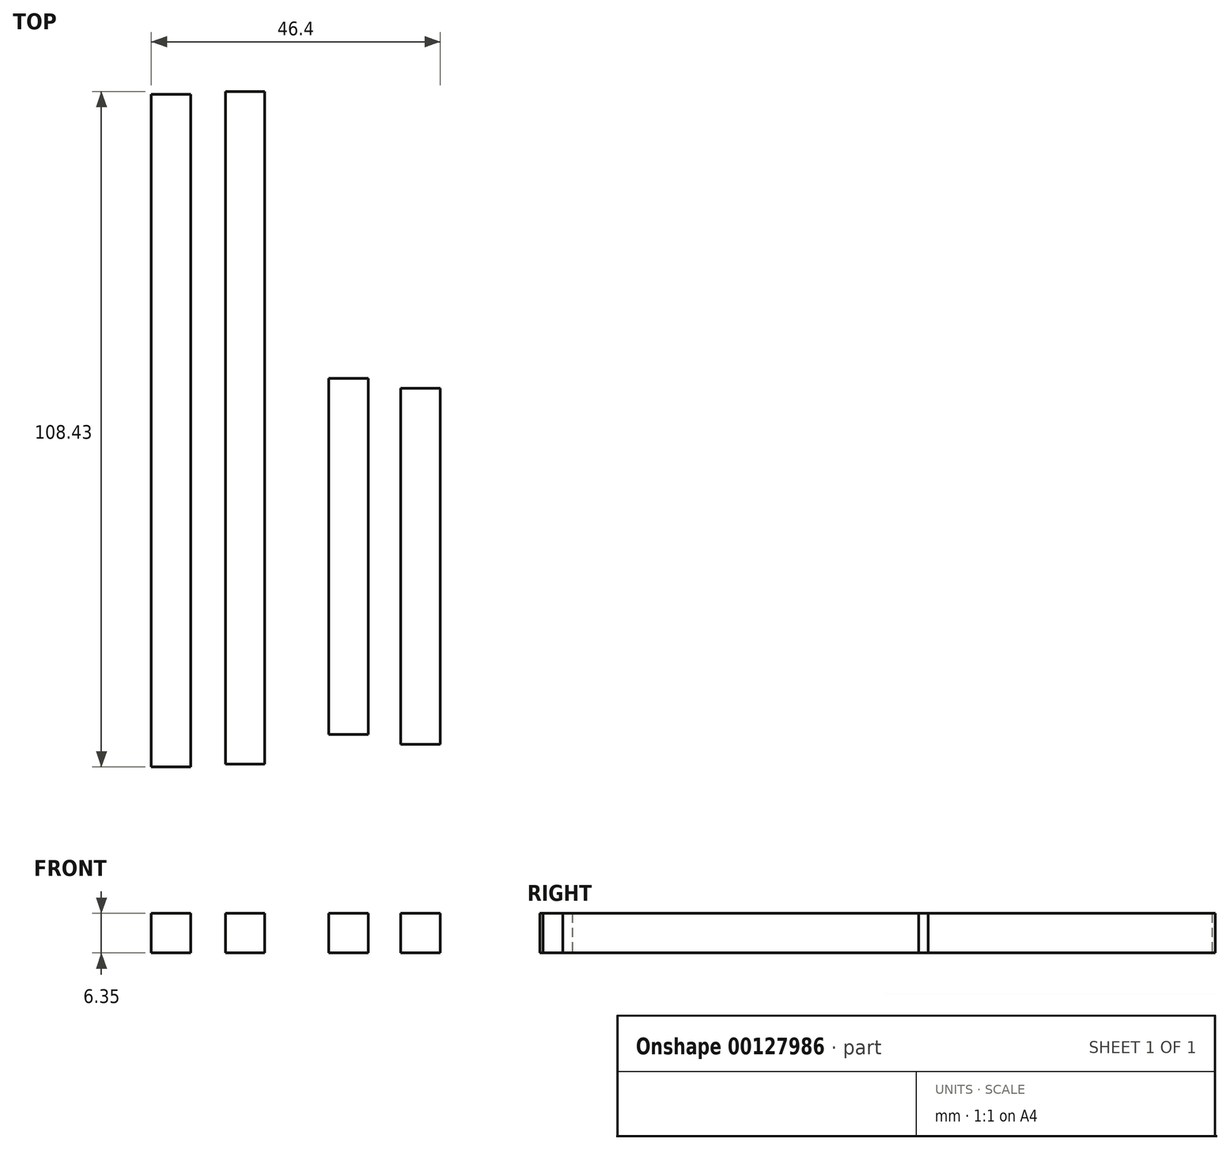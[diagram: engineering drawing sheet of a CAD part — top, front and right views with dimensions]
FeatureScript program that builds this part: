
annotation { "Feature Type Name" : "Feature", "Feature Type Description" : "" }
export const myFeature = defineFeature(function(context is Context, id is Id, definition is map)
    precondition{}
    {
        {
            var Q0;
            Q0=qCreatedBy(makeId("Top.planeOp"),FACE);
            var sketch = newSketch(context, id + "F0", { "sketchPlane" : qUnion([Q0])});
            skLineSegment(sketch, "E0.bottom", {"start": v(-38.1, 104.29) * mm, "end": v(-31.75, 104.29) * mm});
            skLineSegment(sketch, "E0.top", {"start": v(-38.1, -3.66) * mm, "end": v(-31.75, -3.66) * mm});
            skLineSegment(sketch, "E0.left", {"start": v(-38.1, 104.29) * mm, "end": v(-38.1, -3.66) * mm});
            skLineSegment(sketch, "E0.right", {"start": v(-31.75, 104.29) * mm, "end": v(-31.75, -3.66) * mm});
            skLineSegment(sketch, "E1.bottom", {"start": v(-26.21, 104.77) * mm, "end": v(-19.86, 104.77) * mm});
            skLineSegment(sketch, "E1.top", {"start": v(-26.21, -3.18) * mm, "end": v(-19.86, -3.18) * mm});
            skLineSegment(sketch, "E1.left", {"start": v(-26.21, 104.77) * mm, "end": v(-26.21, -3.18) * mm});
            skLineSegment(sketch, "E1.right", {"start": v(-19.86, 104.77) * mm, "end": v(-19.86, -3.18) * mm});
            skLineSegment(sketch, "E2.bottom", {"start": v(-9.6, 58.7) * mm, "end": v(-3.26, 58.7) * mm});
            skLineSegment(sketch, "E2.top", {"start": v(-9.6, 1.55) * mm, "end": v(-3.26, 1.55) * mm});
            skLineSegment(sketch, "E2.left", {"start": v(-9.6, 58.7) * mm, "end": v(-9.6, 1.55) * mm});
            skLineSegment(sketch, "E2.right", {"start": v(-3.26, 58.7) * mm, "end": v(-3.26, 1.55) * mm});
            skLineSegment(sketch, "E3.bottom", {"start": v(1.95, 57.15) * mm, "end": v(8.3, 57.15) * mm});
            skLineSegment(sketch, "E3.top", {"start": v(1.95, 0) * mm, "end": v(8.3, 0) * mm});
            skLineSegment(sketch, "E3.left", {"start": v(1.95, 57.15) * mm, "end": v(1.95, 0) * mm});
            skLineSegment(sketch, "E3.right", {"start": v(8.3, 57.15) * mm, "end": v(8.3, 0) * mm});
            skSolve(sketch);
        }
        {
            var Q0;
            Q0=makeQuery(id+"F0.imprint","IMPRINT",FACE,{"disambiguationData":[TD([[makeQuery(id+"F0.imprint","IMPRINT",EDGE,{"derivedFrom":sQuery(id+"F0.wireOp",EDGE,"E0.bottom")}),-1.0]])]});
            var Q1;
            Q1=makeQuery(id+"F0.imprint","IMPRINT",FACE,{"disambiguationData":[TD([[makeQuery(id+"F0.imprint","IMPRINT",EDGE,{"derivedFrom":sQuery(id+"F0.wireOp",EDGE,"E1.bottom")}),-1.0]])]});
            var Q2;
            Q2=makeQuery(id+"F0.imprint","IMPRINT",FACE,{"disambiguationData":[TD([[makeQuery(id+"F0.imprint","IMPRINT",EDGE,{"derivedFrom":sQuery(id+"F0.wireOp",EDGE,"E2.bottom")}),-1.0]])]});
            var Q3;
            Q3=makeQuery(id+"F0.imprint","IMPRINT",FACE,{"disambiguationData":[TD([[makeQuery(id+"F0.imprint","IMPRINT",EDGE,{"derivedFrom":sQuery(id+"F0.wireOp",EDGE,"E3.bottom")}),-1.0]])]});
            extrude(context, id + "F1", {"entities" : qUnion([Q0, Q1, Q2, Q3]), "depth" : 6.35 * mm});
        }
    });
